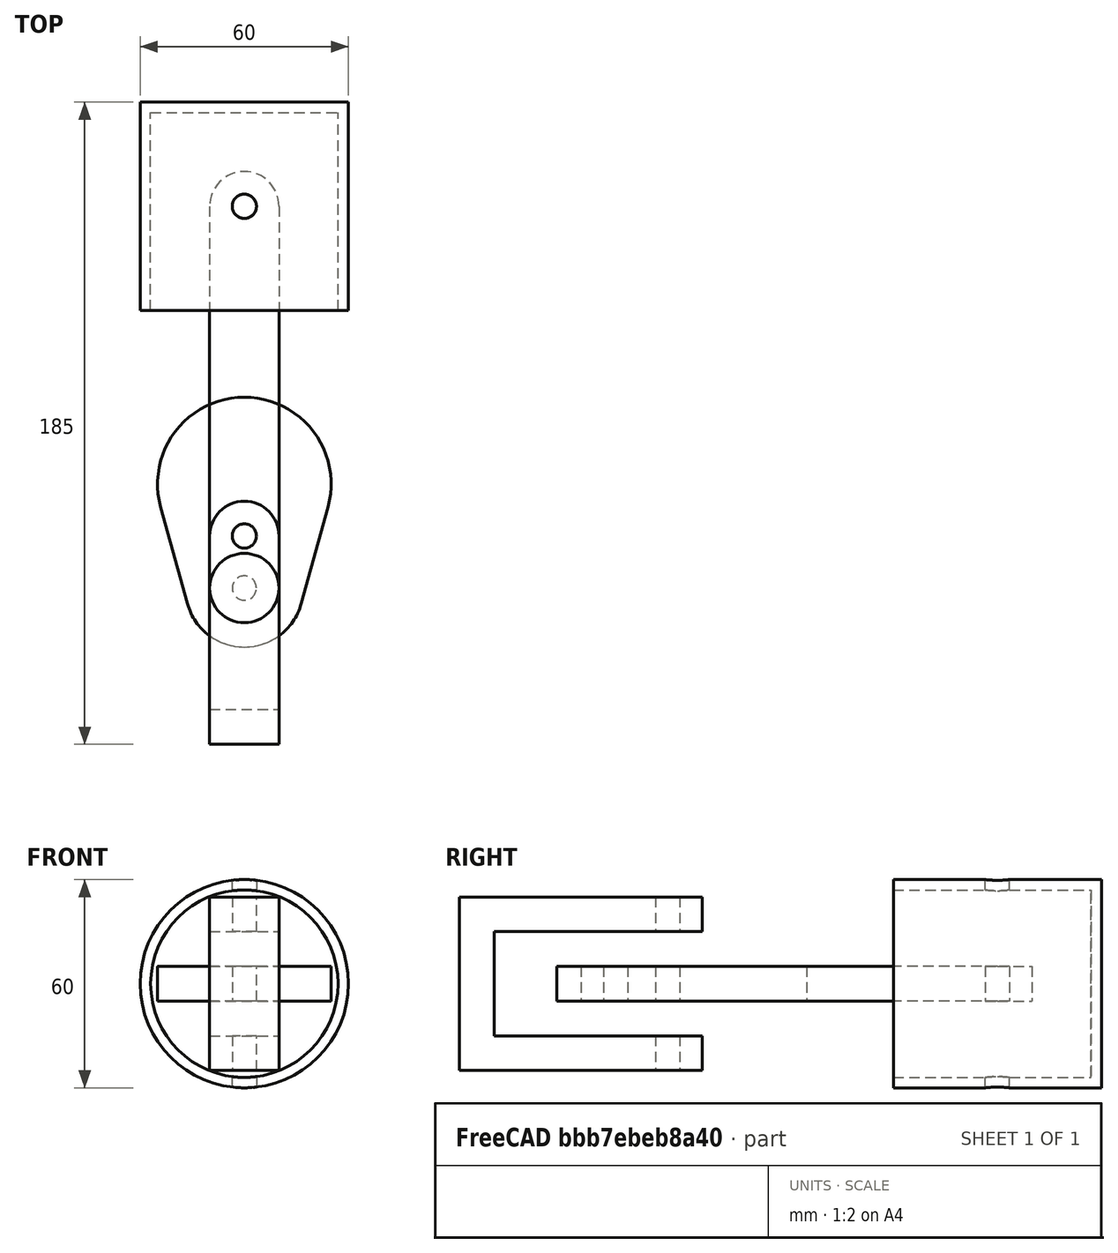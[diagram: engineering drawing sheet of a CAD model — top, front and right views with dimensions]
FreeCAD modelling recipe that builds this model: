
FCSTD DOCUMENT  (FreeCAD 1.0R39319 (Git))
Label: piston head
License: All rights reserved
LicenseURL: https://en.wikipedia.org/wiki/All_rights_reserved
objects: Sketcher::SketchObject×7, App::Link×6, App::FeaturePython×6, PartDesign::SubShapeBinder×4, PartDesign::Body×4, PartDesign::Pad×3, PartDesign::Pocket×2, PartDesign::Revolution×1, Assembly::JointGroup×1, Assembly::AssemblyObject×1
note: 40 computed .brp shape members not serialized (recipe doc carries the construction recipe); baked Part::Feature solids carry a one-line shape summary decoded from their .brp

FEATURE [Sketcher::SketchObject] Sketch  label="mastersketch"
  ArcFitTolerance = 1e-06
  FullyConstrained = true
  MakeInternals = false
  sketch-geometry (20):
    g0: ArcOfCircle CenterX=-7e-16 CenterY=55 CenterZ=0 NormalX=0 NormalY=0 NormalZ=1 AngleXU=0 Radius=10 StartAngle=3e-16 EndAngle=3.14159
    g1: ArcOfCircle CenterX=5e-16 CenterY=-55 CenterZ=0 NormalX=0 NormalY=0 NormalZ=1 AngleXU=0 Radius=10 StartAngle=3.14159 EndAngle=6.28319
    g2: LineSegment StartX=10 StartY=55 StartZ=0 EndX=10 EndY=-55 EndZ=0
    g3: LineSegment StartX=-10 StartY=55 StartZ=0 EndX=-10 EndY=-55 EndZ=0
    g4: Circle CenterX=-7e-16 CenterY=55 CenterZ=0 NormalX=0 NormalY=0 NormalZ=1 AngleXU=0 Radius=3.5
    g5: Circle CenterX=5e-16 CenterY=-55 CenterZ=0 NormalX=0 NormalY=0 NormalZ=1 AngleXU=0 Radius=3.5
    g6: ArcOfCircle CenterX=0 CenterY=-25 CenterZ=0 NormalX=0 NormalY=0 NormalZ=1 AngleXU=0 Radius=25 StartAngle=6.01325 EndAngle=9.69471
    g7: ArcOfCircle CenterX=5e-16 CenterY=-55 CenterZ=0 NormalX=0 NormalY=0 NormalZ=1 AngleXU=0 Radius=17 StartAngle=3.41153 EndAngle=6.01325
    g8: LineSegment StartX=-24.0947 StartY=-31.6667 StartZ=0 EndX=-16.3844 EndY=-59.5333 EndZ=0
    g9: LineSegment StartX=24.0947 StartY=-31.6667 StartZ=0 EndX=16.3844 EndY=-59.5333 EndZ=0
    g10: ArcOfCircle CenterX=0 CenterY=-40 CenterZ=0 NormalX=0 NormalY=0 NormalZ=1 AngleXU=0 Radius=10 StartAngle=6.28318 EndAngle=9.42478
    g11: Circle CenterX=0 CenterY=-40 CenterZ=0 NormalX=0 NormalY=0 NormalZ=1 AngleXU=0 Radius=3.5
    g12: LineSegment StartX=-10 StartY=-55 StartZ=0 EndX=-10 EndY=-100 EndZ=0
    g13: LineSegment StartX=-10 StartY=-100 StartZ=0 EndX=10 EndY=-100 EndZ=0
    g14: LineSegment StartX=10 StartY=-55 StartZ=0 EndX=10 EndY=-100 EndZ=0
    g15: LineSegment StartX=-30 StartY=85 StartZ=0 EndX=-30 EndY=25 EndZ=0
    g16: LineSegment StartX=-30 StartY=25 StartZ=0 EndX=30 EndY=25 EndZ=0
    g17: LineSegment StartX=30 StartY=25 StartZ=0 EndX=30 EndY=85 EndZ=0
    g18: LineSegment StartX=30 StartY=85 StartZ=0 EndX=-30 EndY=85 EndZ=0
    g19: GeomPoint [constr] X=-7e-16 Y=55 Z=0
  constraints (49):
    c: Tangent(g0,g2) = 1.5708
    c: Tangent(g0,g3) = -1.5708
    c: Tangent(g1,g2) = 1.5708
    c: Tangent(g1,g3) = -1.5708
    c: Equal(g0,g1)
    c: Vertical(g3)
    c: Radius(g0) = 10
    c: DistanceY(g1,g0) = 110
    c: Symmetric(g0,g1,g-1)
    c: Coincident(g4,g0)
    c: Coincident(g5,g1)
    c: Diameter(g5) = 7
    c: Diameter(g4) = 7
    c: PointOnObject(g6,g-2)
    c: Coincident(g7,g1)
    c: Tangent(g8,g6) = -1.5708
    c: Tangent(g8,g7) = -1.5708
    c: Tangent(g9,g6) = 1.5708
    c: Tangent(g9,g7) = 1.5708
    c: DistanceY(g1,g6) = 30
    c: Radius(g6) = 25
    c: Radius(g7) = 17
    c: PointOnObject(g10,g-2)
    c: PointOnObject(g10,g3)
    c: PointOnObject(g10,g2)
    c: Coincident(g11,g10)
    c: Diameter(g11) = 7
    c: Radius(g10) = 10
    c: DistanceY(g10,g6) = 15
    c: Coincident(g12,g1)
    c: Vertical(g12)
    c: Coincident(g13,g12)
    c: Horizontal(g13)
    c: Coincident(g14,g1)
    c: Coincident(g14,g13)
    c: Vertical(g14)
    c: Distance(g10,g13) = 60
    c: Coincident(g15,g16)
    c: Coincident(g16,g17)
    c: Coincident(g17,g18)
    c: Coincident(g18,g15)
    c: Vertical(g15)
    c: Vertical(g17)
    c: Horizontal(g16)
    c: Horizontal(g18)
    c: Symmetric(g17,g15,g19)
    c: Coincident(g19,g0)
    c: DistanceX(g18,g18) = 60
    c: Equal(g18,g15)
FEATURE [PartDesign::SubShapeBinder] Binder
  BindCopyOnChange = 0
  BindMode = 0
  ClaimChildren = false
  Context = -> Body [Binder.]
  Fuse = false
  MakeFace = true
  OffsetFill = false
  OffsetIntersection = false
  OffsetJoinType = 0
  OffsetOpenResult = false
  PartialLoad = false
  Refine = true
  Relative = true
  Support = -> [Sketch]
  _Version = 2
FEATURE [Sketcher::SketchObject] Sketch001
  ArcFitTolerance = 1e-06
  AttachmentSupport = -> [XY_Plane]
  ExternalGeometry = -> [Binder]
  FullyConstrained = true
  MakeInternals = false
  MapMode = 5
  sketch-geometry (6):
    g0: LineSegment StartX=-10 StartY=55 StartZ=0 EndX=-10 EndY=-55 EndZ=0
    g1: LineSegment StartX=10 StartY=55 StartZ=0 EndX=10 EndY=-55 EndZ=0
    g2: Circle CenterX=-4e-16 CenterY=55 CenterZ=0 NormalX=0 NormalY=0 NormalZ=1 AngleXU=0 Radius=3.5
    g3: Circle CenterX=7e-16 CenterY=-55 CenterZ=0 NormalX=0 NormalY=0 NormalZ=1 AngleXU=0 Radius=3.5
    g4: ArcOfCircle CenterX=7e-16 CenterY=-55 CenterZ=0 NormalX=0 NormalY=0 NormalZ=1 AngleXU=0 Radius=10 StartAngle=3.14159 EndAngle=6.28319
    g5: ArcOfCircle CenterX=-4e-16 CenterY=55 CenterZ=0 NormalX=0 NormalY=0 NormalZ=1 AngleXU=0 Radius=10 StartAngle=6.28318 EndAngle=9.42478
  constraints (14):
    c: Coincident(g-4,g0)
    c: Coincident(g0,g-5)
    c: Coincident(g-6,g1)
    c: Coincident(g1,g-6)
    c: Coincident(g4,g3)
    c: Coincident(g4,g0)
    c: Coincident(g4,g1)
    c: Equal(g-7,g2)
    c: Equal(g-8,g3)
    c: Equal(g4,g-5)
    c: Coincident(g5,g2)
    c: Coincident(g5,g0)
    c: Coincident(g5,g1)
    c: Equal(g-3,g5)
FEATURE [PartDesign::Pad] Pad
  Direction = (0,0,1)
  Length = 10
  Length2 = 10
  Midplane = true
  Profile = -> Sketch001
  ReferenceAxis = -> Sketch001 [N_Axis]
  Refine = true
  Suppressed = false
  Type = 0
FEATURE [PartDesign::Body] Body  label="link"
  AllowCompound = false
  Group = -> [Binder,Sketch001,Pad]
  Origin = -> Origin
  Tip = -> Pad
FEATURE [PartDesign::SubShapeBinder] Binder001
  BindCopyOnChange = 0
  BindMode = 0
  ClaimChildren = false
  Context = -> Body001 [Binder001.]
  Fuse = false
  MakeFace = true
  OffsetFill = false
  OffsetIntersection = false
  OffsetJoinType = 0
  OffsetOpenResult = false
  PartialLoad = false
  Refine = true
  Relative = true
  Support = -> [Sketch]
  _Version = 2
FEATURE [Sketcher::SketchObject] Sketch002
  ArcFitTolerance = 1e-06
  AttachmentSupport = -> [XY_Plane001]
  ExternalGeometry = -> [Binder001]
  FullyConstrained = true
  MakeInternals = false
  MapMode = 5
  sketch-geometry (6):
    g0: LineSegment StartX=0 StartY=85 StartZ=0 EndX=-30 EndY=85 EndZ=0
    g1: LineSegment StartX=-30 StartY=85 StartZ=0 EndX=-30 EndY=25 EndZ=0
    g2: LineSegment StartX=-27 StartY=25 StartZ=0 EndX=-27 EndY=82 EndZ=0
    g3: LineSegment StartX=-27 StartY=82 StartZ=0 EndX=0 EndY=82 EndZ=0
    g4: LineSegment StartX=0 StartY=82 StartZ=0 EndX=0 EndY=85 EndZ=0
    g5: LineSegment StartX=-30 StartY=25 StartZ=0 EndX=-27 EndY=25 EndZ=0
  constraints (15):
    c: Symmetric(g-3,g-3,g0)
    c: Coincident(g0,g-4)
    c: Coincident(g1,g0)
    c: Coincident(g1,g-5)
    c: Vertical(g2)
    c: Coincident(g3,g2)
    c: PointOnObject(g3,g-2)
    c: Horizontal(g3)
    c: Coincident(g4,g3)
    c: Coincident(g4,g0)
    c: DistanceY(g4,g4) = 3
    c: DistanceX(g1,g2) = 3
    c: PointOnObject(g2,g-5)
    c: Coincident(g5,g1)
    c: Coincident(g5,g2)
FEATURE [PartDesign::Revolution] Revolution
  Angle = 360
  Angle2 = 60
  Axis = (0,1,0)
  Base = (0,0,0)
  Profile = -> Sketch002
  ReferenceAxis = -> Sketch002 [V_Axis]
  Refine = true
  Suppressed = false
  Type = 0
FEATURE [Sketcher::SketchObject] Sketch003
  ArcFitTolerance = 1e-06
  AttachmentSupport = -> [XY_Plane001]
  ExternalGeometry = -> [Binder001]
  FullyConstrained = true
  MakeInternals = false
  MapMode = 5
  sketch-geometry (1):
    g0: Circle CenterX=0 CenterY=55 CenterZ=0 NormalX=0 NormalY=0 NormalZ=1 AngleXU=0 Radius=3.5
  constraints (2):
    c: Coincident(g0,g-3)
    c: Equal(g0,g-3)
FEATURE [PartDesign::Pocket] Pocket
  BaseFeature = -> Revolution
  Direction = (0,0,-1)
  Length = 4
  Length2 = 5
  Midplane = true
  Profile = -> Sketch003
  ReferenceAxis = -> Sketch003 [N_Axis]
  Refine = true
  Suppressed = false
  Type = 1
FEATURE [PartDesign::Body] Body001  label="piston head"
  AllowCompound = false
  Group = -> [Binder001,Sketch002,Revolution,Sketch003,Pocket]
  Origin = -> Origin001
  Tip = -> Pocket
FEATURE [PartDesign::SubShapeBinder] Binder002
  BindCopyOnChange = 0
  BindMode = 0
  ClaimChildren = false
  Context = -> Body002 [Binder002.]
  Fuse = false
  MakeFace = false
  OffsetFill = false
  OffsetIntersection = false
  OffsetJoinType = 0
  OffsetOpenResult = false
  PartialLoad = false
  Refine = true
  Relative = true
  Support = -> [Sketch]
  _Version = 2
FEATURE [Sketcher::SketchObject] Sketch004
  ArcFitTolerance = 1e-06
  AttachmentSupport = -> [XY_Plane002]
  ExternalGeometry = -> [Binder002]
  FullyConstrained = true
  MakeInternals = false
  MapMode = 5
  sketch-geometry (6):
    g0: Circle CenterX=0 CenterY=-40 CenterZ=0 NormalX=0 NormalY=0 NormalZ=1 AngleXU=0 Radius=3.5
    g1: Circle CenterX=0 CenterY=-55 CenterZ=0 NormalX=0 NormalY=0 NormalZ=1 AngleXU=0 Radius=3.5
    g2: LineSegment StartX=-24.0947 StartY=-31.6667 StartZ=0 EndX=-16.3844 EndY=-59.5333 EndZ=0
    g3: ArcOfCircle CenterX=-2.1e-15 CenterY=-55 CenterZ=0 NormalX=0 NormalY=0 NormalZ=1 AngleXU=0 Radius=17 StartAngle=3.41153 EndAngle=6.01325
    g4: LineSegment StartX=16.3844 StartY=-59.5333 StartZ=0 EndX=24.0947 EndY=-31.6667 EndZ=0
    g5: ArcOfCircle CenterX=-7e-16 CenterY=-25 CenterZ=0 NormalX=0 NormalY=0 NormalZ=1 AngleXU=0 Radius=25 StartAngle=6.01325 EndAngle=9.69471
  constraints (12):
    c: Coincident(g0,g-8)
    c: Equal(g0,g-8)
    c: Coincident(g1,g-7)
    c: Equal(g1,g-7)
    c: Coincident(g-4,g2)
    c: Coincident(g2,g-5)
    c: Tangent(g2,g3) = -1.5708
    c: Coincident(g3,g-6)
    c: Tangent(g3,g4) = -1.5708
    c: Tangent(g4,g5) = -1.5708
    c: Coincident(g5,g2)
    c: Equal(g5,g-3)
FEATURE [PartDesign::Pad] Pad001
  Direction = (0,0,1)
  Length = 10
  Length2 = 10
  Midplane = true
  Profile = -> Sketch004
  ReferenceAxis = -> Sketch004 [N_Axis]
  Refine = true
  Suppressed = false
  Type = 0
FEATURE [PartDesign::Body] Body002  label="crank"
  AllowCompound = false
  Group = -> [Binder002,Sketch004,Pad001]
  Origin = -> Origin002
  Tip = -> Pad001
FEATURE [PartDesign::SubShapeBinder] Binder003
  BindCopyOnChange = 0
  BindMode = 0
  ClaimChildren = false
  Context = -> Body003 [Binder003.]
  Fuse = false
  MakeFace = false
  OffsetFill = false
  OffsetIntersection = false
  OffsetJoinType = 0
  OffsetOpenResult = false
  PartialLoad = false
  Refine = true
  Relative = true
  Support = -> [Sketch]
  _Version = 2
FEATURE [Sketcher::SketchObject] Sketch005
  ArcFitTolerance = 1e-06
  AttachmentSupport = -> [XY_Plane003]
  ExternalGeometry = -> [Binder003]
  FullyConstrained = true
  MakeInternals = false
  MapMode = 5
  sketch-geometry (7):
    g0: LineSegment StartX=-10 StartY=-55 StartZ=0 EndX=-10 EndY=-100 EndZ=0
    g1: LineSegment StartX=-10 StartY=-100 StartZ=0 EndX=10 EndY=-100 EndZ=0
    g2: LineSegment StartX=10 StartY=-55 StartZ=0 EndX=10 EndY=-100 EndZ=0
    g3: LineSegment StartX=10 StartY=-40 StartZ=0 EndX=10 EndY=-55 EndZ=0
    g4: LineSegment StartX=-10 StartY=-40 StartZ=0 EndX=-10 EndY=-55 EndZ=0
    g5: Circle CenterX=-1.2e-15 CenterY=-40 CenterZ=0 NormalX=0 NormalY=0 NormalZ=1 AngleXU=0 Radius=3.5
    g6: ArcOfCircle CenterX=-1.2e-15 CenterY=-40 CenterZ=0 NormalX=0 NormalY=0 NormalZ=1 AngleXU=0 Radius=10 StartAngle=-1.52967e-10 EndAngle=3.14159
  constraints (14):
    c: Coincident(g0,g-7)
    c: Coincident(g0,g-5)
    c: Coincident(g1,g0)
    c: Coincident(g1,g-4)
    c: Coincident(g2,g-8)
    c: Coincident(g2,g1)
    c: Coincident(g3,g-6)
    c: Coincident(g3,g2)
    c: Coincident(g4,g-6)
    c: Coincident(g4,g0)
    c: Tangent(g4,g6) = -1.5708
    c: Coincident(g6,g3)
    c: Coincident(g5,g6)
    c: Equal(g-9,g5)
FEATURE [PartDesign::Pad] Pad002
  Direction = (0,0,1)
  Length = 50
  Length2 = 10
  Midplane = true
  Profile = -> Sketch005
  ReferenceAxis = -> Sketch005 [N_Axis]
  Refine = true
  Suppressed = false
  Type = 0
FEATURE [Sketcher::SketchObject] Sketch006
  ArcFitTolerance = 1e-06
  AttachmentSupport = -> [Pad002]
  ExternalGeometry = -> [Pad002]
  FullyConstrained = true
  MakeInternals = false
  MapMode = 5
  Placement = pos=(-10,4.689e-13,0) rot=(-0.57735,0.57735,0.57735;4.18879rad)
  sketch-geometry (4):
    g0: LineSegment StartX=25 StartY=15 StartZ=0 EndX=25 EndY=-15 EndZ=0
    g1: LineSegment StartX=25 StartY=-15 StartZ=0 EndX=90 EndY=-15 EndZ=0
    g2: LineSegment StartX=90 StartY=-15 StartZ=0 EndX=90 EndY=15 EndZ=0
    g3: LineSegment StartX=90 StartY=15 StartZ=0 EndX=25 EndY=15 EndZ=0
  constraints (12):
    c: Coincident(g0,g1)
    c: Coincident(g1,g2)
    c: Coincident(g2,g3)
    c: Coincident(g3,g0)
    c: Vertical(g0)
    c: Vertical(g2)
    c: Horizontal(g1)
    c: Horizontal(g3)
    c: Distance(g-4,g3) = 10
    c: Distance(g1,g3) = 30
    c: Distance(g-3,g2) = 10
    c: DistanceX(g3,g3) = 65
FEATURE [PartDesign::Pocket] Pocket001
  BaseFeature = -> Pad002
  Direction = (1,-4.67e-14,-1e-16)
  Length = 10
  Length2 = 5
  Midplane = true
  Profile = -> Sketch006
  ReferenceAxis = -> Sketch006 [N_Axis]
  Refine = true
  Suppressed = false
  Type = 1
FEATURE [PartDesign::Body] Body003  label="mmount"
  AllowCompound = false
  Group = -> [Binder003,Sketch005,Pad002,Sketch006,Pocket001]
  Origin = -> Origin003
  Tip = -> Pocket001
FEATURE [App::Link] mmount  label="mmount001"
  LinkedObject = -> Body003
FEATURE [App::Link] mmount001  label="mmount002"
  LinkedObject = -> Body003
FEATURE [App::FeaturePython] GroundedJoint  # Assembly grounded joint (typed FeaturePython)
  ObjectToGround = -> mmount001
FEATURE [App::Link] crank  label="crank001"
  LinkPlacement = pos=(1.17e-14,-80,-8) rot=(0,0,1;3.14159rad)
  LinkedObject = -> Body002
  Placement = pos=(1.17e-14,-80,-8) rot=(0,0,1;3.14159rad)
FEATURE [App::Link] crank001  label="crank002"
  LinkPlacement = pos=(1.17e-14,-80,10) rot=(0,0,1;3.14159rad)
  LinkedObject = -> Body002
  Placement = pos=(1.17e-14,-80,10) rot=(0,0,1;3.14159rad)
FEATURE [App::FeaturePython] Joint  label="Revolute"  # Assembly joint (typed FeaturePython)
  Activated = true
  AngleMax = 0
  AngleMin = 0
  Detach1 = false
  Detach2 = false
  Distance = 0
  Distance2 = 0
  EnableAngleMax = false
  EnableAngleMin = false
  EnableLengthMax = false
  EnableLengthMin = false
  JointType = 1 (Revolute)
  LengthMax = 0
  LengthMin = 0
  Offset2 = pos=(0,0,10) rot=(0,0,1;0rad)
  Placement1 = pos=(0,-40,-5) rot=(0,0,1;0rad)
  Placement2 = pos=(-1.2e-15,-40,5) rot=(1,0,0;3.14159rad)
  Reference1 = -> Assembly [crank001.Edge17,crank001.Edge17]
  Reference2 = -> Assembly [mmount001.Edge28,mmount001.Edge28]
FEATURE [App::Link] link  label="link001"
  LinkPlacement = pos=(-6.8e-15,30,4e-16) rot=(0,0,1;0rad)
  LinkedObject = -> Body
  Placement = pos=(-6.8e-15,30,4e-16) rot=(0,0,1;0rad)
FEATURE [App::FeaturePython] Joint001  label="Revolute001"  # Assembly joint (typed FeaturePython)
  Activated = true
  AngleMax = 0
  AngleMin = 0
  Detach1 = false
  Detach2 = false
  Distance = 0
  Distance2 = 0
  EnableAngleMax = false
  EnableAngleMin = false
  EnableLengthMax = false
  EnableLengthMin = false
  JointType = 1 (Revolute)
  LengthMax = 0
  LengthMin = 0
  Offset2 = pos=(0,0,-10) rot=(0,0,1;0rad)
  Placement1 = pos=(7e-16,-55,-5) rot=(0,0,1;0rad)
  Placement2 = pos=(0,-55,-15) rot=(0,0,1;0rad)
  Reference1 = -> Assembly [link.Edge14,link.Edge14]
  Reference2 = -> Assembly [crank001.Edge14,crank001.Edge14]
FEATURE [App::FeaturePython] Joint002  label="Fixed"  # Assembly joint (typed FeaturePython)
  Activated = true
  AngleMax = 0
  AngleMin = 0
  Detach1 = false
  Detach2 = false
  Distance = 0
  Distance2 = 0
  EnableAngleMax = false
  EnableAngleMin = false
  EnableLengthMax = false
  EnableLengthMin = false
  JointType = 0 (Fixed)
  LengthMax = 0
  LengthMin = 0
  Offset2 = pos=(0,0,-18) rot=(0,0,1;0rad)
  Placement1 = pos=(0,-33.696,-5) rot=(0,0,1;0rad)
  Placement2 = pos=(0,-33.696,-23) rot=(0,0,1;0rad)
  Reference1 = -> Assembly [crank.Face7,crank.Face7]
  Reference2 = -> Assembly [crank001.Face7,crank001.Face7]
FEATURE [App::Link] piston_head  label="piston head001"
  LinkPlacement = pos=(-7.1e-15,139.785,1.80481) rot=(0,-0.003763,0.999993;3.14159rad)
  LinkedObject = -> Body001
  Placement = pos=(-7.1e-15,139.785,1.80481) rot=(0,-0.003763,0.999993;3.14159rad)
FEATURE [App::FeaturePython] Joint003  label="Revolute002"  # Assembly joint (typed FeaturePython)
  Activated = true
  AngleMax = 0
  AngleMin = 0
  Detach1 = false
  Detach2 = false
  Distance = 0
  Distance2 = 0
  EnableAngleMax = false
  EnableAngleMin = false
  EnableLengthMax = false
  EnableLengthMin = false
  JointType = 1 (Revolute)
  LengthMax = 0
  LengthMin = 0
  Offset2 = pos=(0,0,-27) rot=(0,0,1;0rad)
  Placement1 = pos=(0,55,-28.3917) rot=(0,0,1;0rad)
  Placement2 = pos=(-4e-16,55,-27) rot=(0,0,1;0rad)
  Reference1 = -> Assembly [piston_head.Face4,piston_head.Face4]
  Reference2 = -> Assembly [link.Face6,link.Face6]
FEATURE [App::FeaturePython] Joint004  label="Slider"  # Assembly joint (typed FeaturePython)
  Activated = true
  AngleMax = 0
  AngleMin = 0
  Detach1 = false
  Detach2 = false
  Distance = 0
  Distance2 = 0
  EnableAngleMax = false
  EnableAngleMin = false
  EnableLengthMax = false
  EnableLengthMin = false
  JointType = 3 (Slider)
  LengthMax = 0
  LengthMin = 0
  Placement1 = pos=(-7.1e-15,85,-3.1e-15) rot=(1,0,0;1.5708rad)
  Placement2 = pos=(0,-100,-2e-16) rot=(-1,0,0;1.5708rad)
  Reference1 = -> Assembly [piston_head.Face1,piston_head.Face1]
  Reference2 = -> Assembly [mmount001.Face1,mmount001.Face1]
FEATURE [Assembly::JointGroup] Joints
  Group = -> [GroundedJoint,Joint,Joint001,Joint002,Joint003,Joint004]
FEATURE [Assembly::AssemblyObject] Assembly
  Group = -> [Joints,mmount001,GroundedJoint,crank,crank001,Joint,link,Joint001,Joint002,piston_head,Joint003,Joint004]
  Origin = -> Origin004
  Type = Assembly
